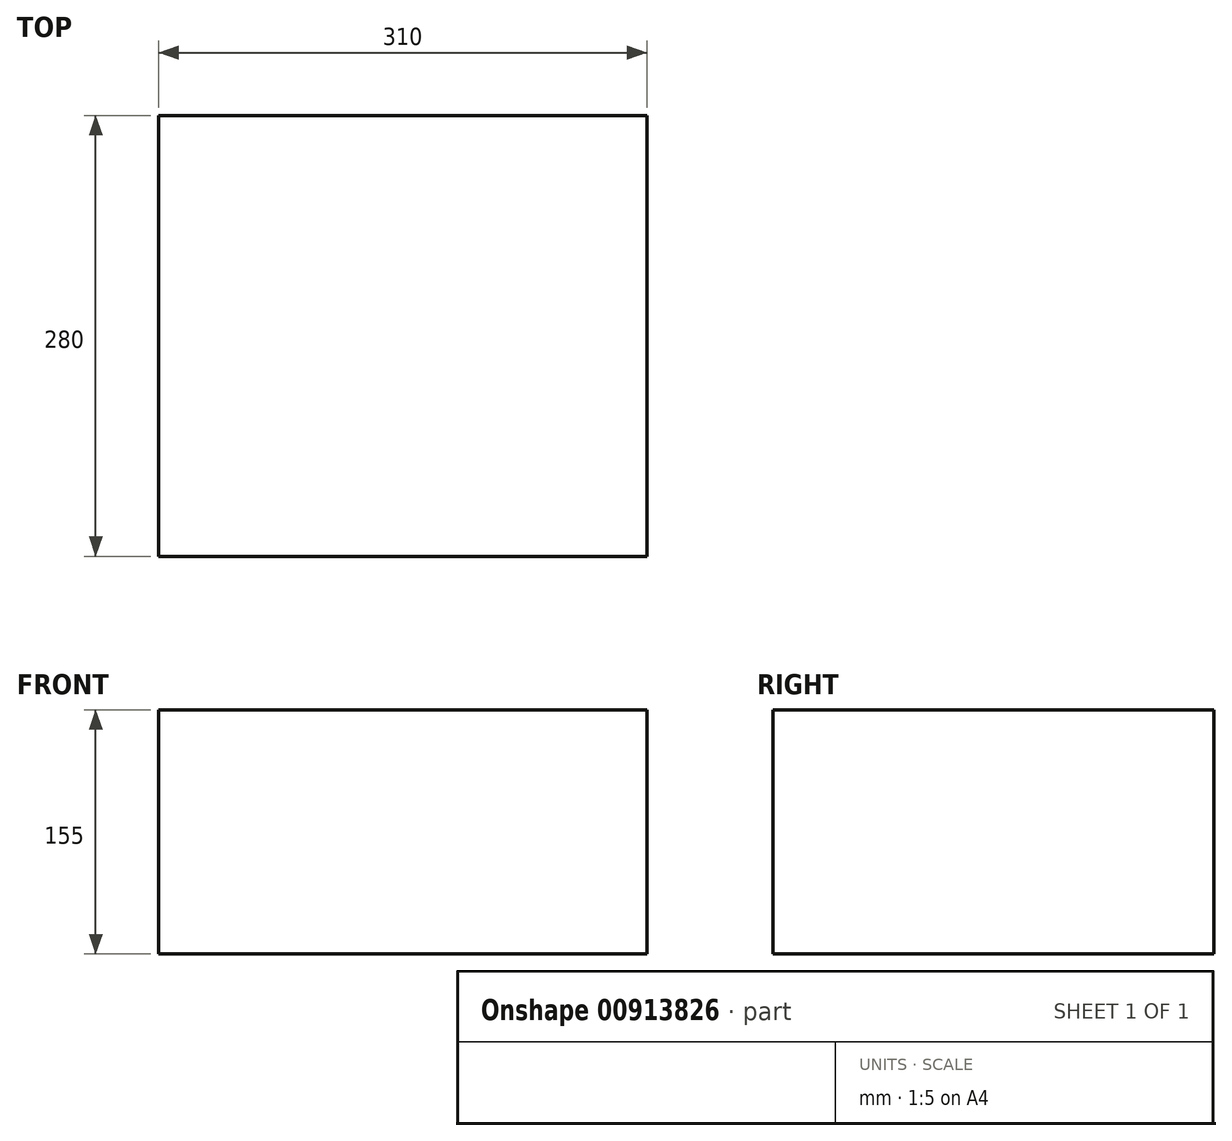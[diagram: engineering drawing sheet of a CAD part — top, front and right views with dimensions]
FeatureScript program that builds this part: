
annotation { "Feature Type Name" : "Feature", "Feature Type Description" : "" }
export const myFeature = defineFeature(function(context is Context, id is Id, definition is map)
    precondition{}
    {
        {
            var Q0;
            Q0=qCreatedBy(makeId("Top.planeOp"),FACE);
            var sketch = newSketch(context, id + "F0", { "sketchPlane" : qUnion([Q0])});
            skLineSegment(sketch, "E0.bottom", {"start": v(155, -140) * mm, "end": v(-155, -140) * mm});
            skLineSegment(sketch, "E0.top", {"start": v(155, 140) * mm, "end": v(-155, 140) * mm});
            skLineSegment(sketch, "E0.left", {"start": v(155, -140) * mm, "end": v(155, 140) * mm});
            skLineSegment(sketch, "E0.right", {"start": v(-155, -140) * mm, "end": v(-155, 140) * mm});
            skPoint(sketch, "E0.middle", {"position": v(0, 0) * mm});
            skSolve(sketch);
        }
        {
            var Q0;
            Q0=makeQuery(id+"F0.imprint","IMPRINT",FACE,{"disambiguationData":[TD([[makeQuery(id+"F0.imprint","IMPRINT",EDGE,{"derivedFrom":sQuery(id+"F0.wireOp",EDGE,"E0.bottom")}),-1.0]])]});
            extrude(context, id + "F1", {"entities" : qUnion([Q0]), "depth" : 155 * mm, "offsetDistance" : 25 * mm});
        }
    });
